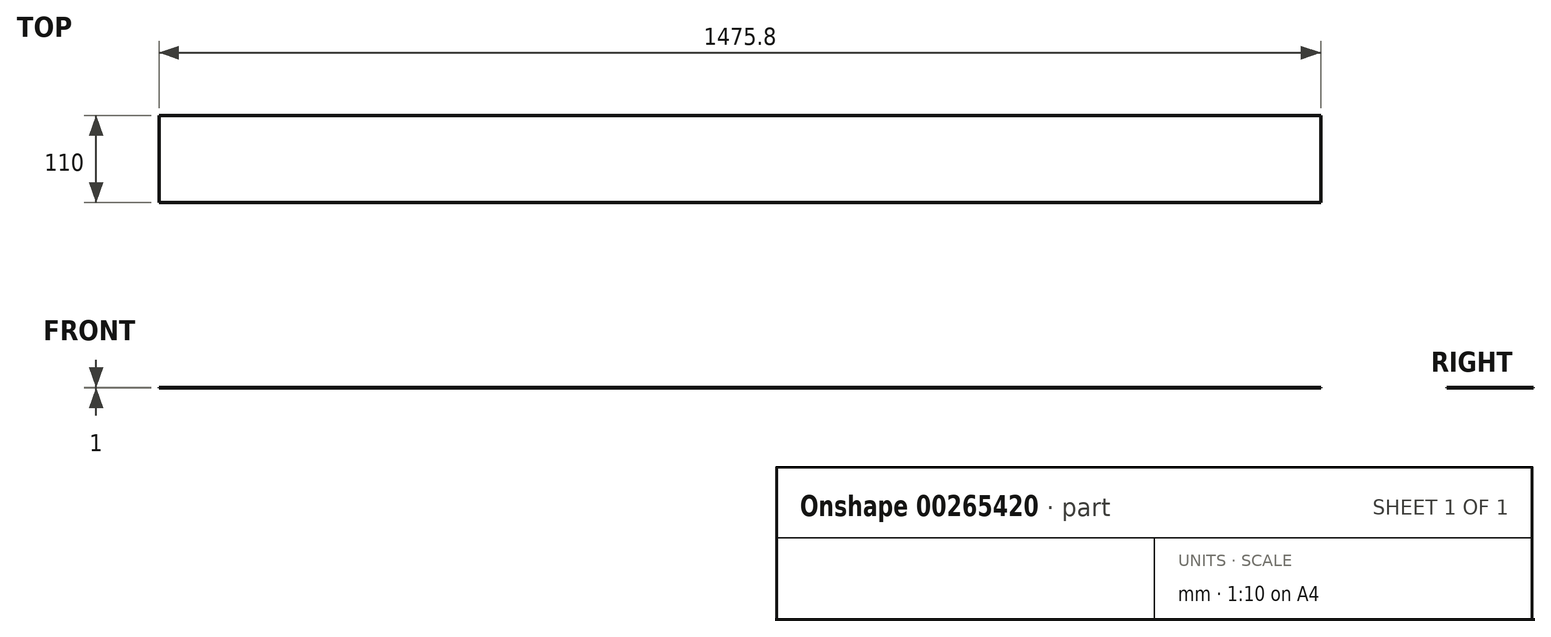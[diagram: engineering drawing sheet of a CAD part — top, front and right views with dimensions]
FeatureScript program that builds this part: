
annotation { "Feature Type Name" : "Feature", "Feature Type Description" : "" }
export const myFeature = defineFeature(function(context is Context, id is Id, definition is map)
    precondition{}
    {
        {
            var Q0;
            Q0=qCreatedBy(makeId("Top.planeOp"),FACE);
            var sketch = newSketch(context, id + "F0", { "sketchPlane" : qUnion([Q0])});
            skLineSegment(sketch, "E0.bottom", {"start": v(-1372.4, 120.14) * mm, "end": v(103.4, 120.14) * mm});
            skLineSegment(sketch, "E0.top", {"start": v(-1372.4, 10.14) * mm, "end": v(103.4, 10.14) * mm});
            skLineSegment(sketch, "E0.left", {"start": v(-1372.4, 120.14) * mm, "end": v(-1372.4, 10.14) * mm});
            skLineSegment(sketch, "E0.right", {"start": v(103.4, 120.14) * mm, "end": v(103.4, 10.14) * mm});
            skLineSegment(sketch, "E1.bottom", {"start": v(-544.5, 120.14) * mm, "end": v(-634.5, 120.14) * mm, "construction": true});
            skLineSegment(sketch, "E1.top", {"start": v(-544.5, 10.14) * mm, "end": v(-634.5, 10.14) * mm, "construction": true});
            skLineSegment(sketch, "E1.left", {"start": v(-634.5, 120.14) * mm, "end": v(-634.5, 10.14) * mm, "construction": true});
            skSolve(sketch);
        }
        {
            var Q0;
            Q0=makeQuery(id+"F0.imprint","IMPRINT",FACE,{"disambiguationData":[TD([[makeQuery(id+"F0.imprint","IMPRINT",EDGE,{"derivedFrom":sQuery(id+"F0.wireOp",EDGE,"E0.bottom")}),-1.0]])]});
            extrude(context, id + "F1", {"entities" : qUnion([Q0]), "depth" : 1 * mm});
        }
    });
